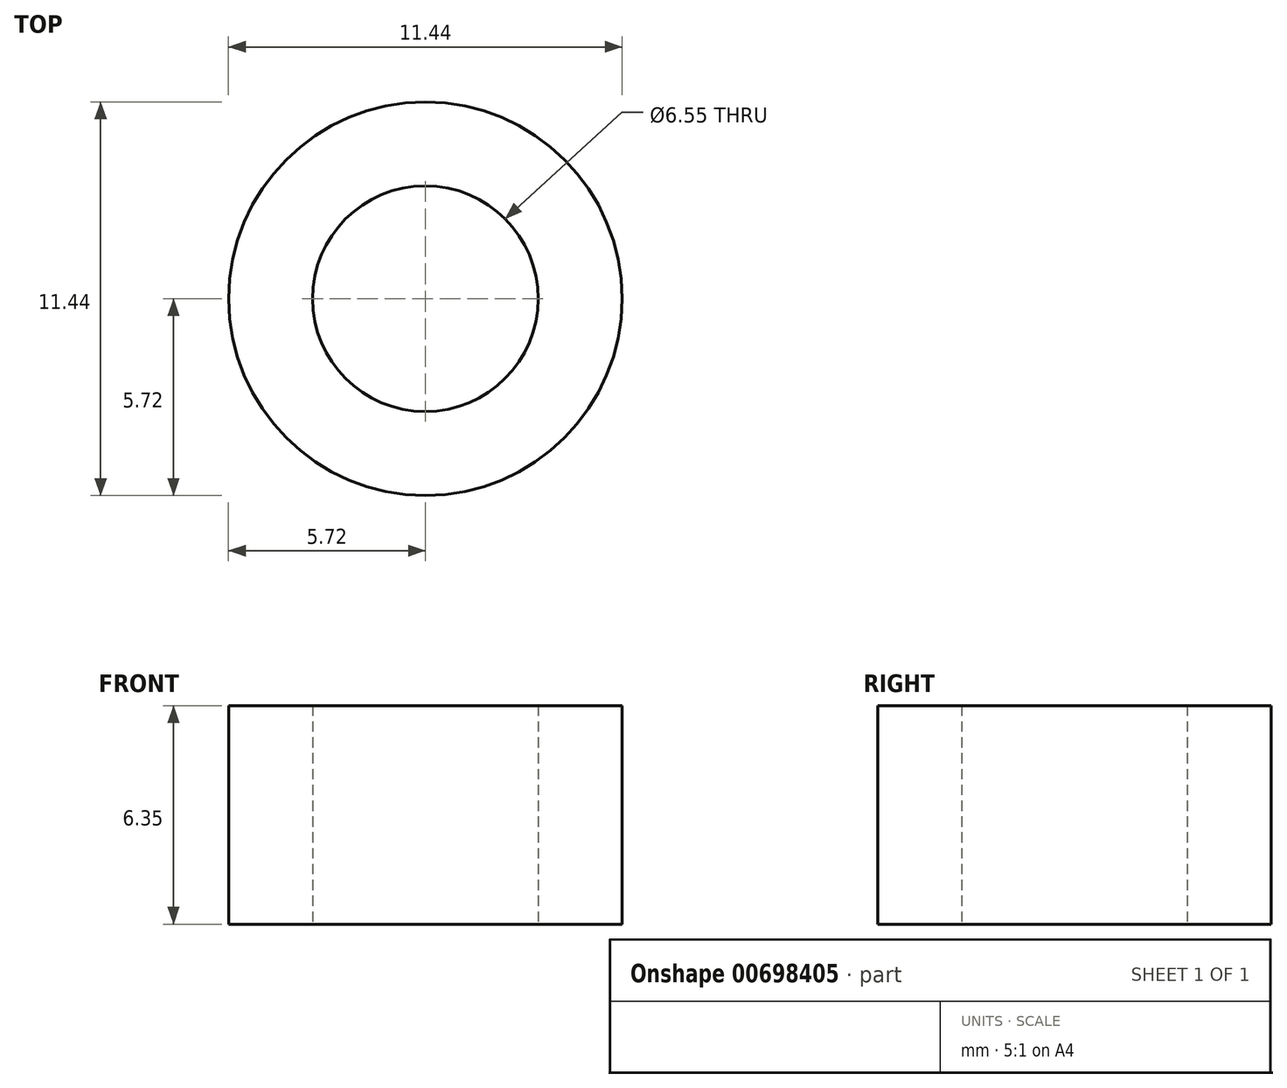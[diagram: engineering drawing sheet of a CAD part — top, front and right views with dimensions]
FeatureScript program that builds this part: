
annotation { "Feature Type Name" : "Feature", "Feature Type Description" : "" }
export const myFeature = defineFeature(function(context is Context, id is Id, definition is map)
    precondition{}
    {
        {
            var Q0;
            Q0=qCreatedBy(makeId("Top.planeOp"),FACE);
            var sketch = newSketch(context, id + "F0", { "sketchPlane" : qUnion([Q0])});
            skCircle(sketch, "E0", {"center": v(0, 0) * mm, "radius": 5.72 * mm});
            skCircle(sketch, "E1", {"center": v(0, 0) * mm, "radius": 3.28 * mm});
            skSolve(sketch);
        }
        {
            var Q0;
            Q0 = qSketchRegion(id + "F0", true);
            extrude(context, id + "F1", {"entities" : qUnion([Q0]), "depth" : 6.35 * mm, "offsetDistance" : 25.4 * mm});
        }
    });
